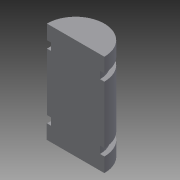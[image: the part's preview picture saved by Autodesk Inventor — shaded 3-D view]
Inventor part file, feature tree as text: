
AUTODESK INVENTOR PART (.ipt)
format: ipt  version: 2015 (Build 190159000, 159)  size: 97,280 bytes
history: native  units: mm
features: extrude x6, sketch x6
ambient origin geometry x8: Origin, YZ Plane, XZ Plane, XY Plane, X Axis, Y Axis, Z Axis, Center Point
bodies: Solid1 (feature_tree)
feature tree (12):
  extrude  "Extrusion1"  Depth=5.0mm TaperAngle=0.0deg
  extrude  "Extrusion2"  Depth=2.5mm TaperAngle=0.0deg
  extrude  "Extrusion3"  Depth=2.5mm TaperAngle=0.0deg
  extrude  "Extrusion4"  Depth=35.0mm TaperAngle=0.0deg
  extrude  "Extrusion5"  [1 undecoded]
  extrude  "Extrusion6"  [1 undecoded]
  sketch  "Sketch1"  dims[d0=20.0mm d1=5.0mm d2=0.0mm]
  sketch  "Sketch2"  dims[d3=17.0mm d4=2.5mm d5=0.0mm]
  sketch  "Sketch3"  dims[d6=20.0mm d7=0.0mm d8=2.5mm d9=0.0mm]
  sketch  "Sketch4"  dims[d10=5.0mm d11=0.0mm d12=35.0mm d13=0.0mm]
  sketch  "Sketch5"
  sketch  "Sketch6"
note: 2 required parameter values undecoded (feature->parameter linkage not recoverable at this tier; creation-order binding heuristic only, values carry confidence <= 0.55)
